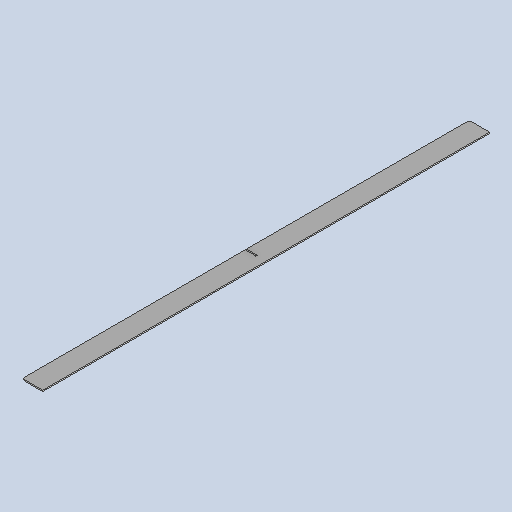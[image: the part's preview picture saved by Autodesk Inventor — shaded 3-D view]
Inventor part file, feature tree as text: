
AUTODESK INVENTOR PART (.ipt)
format: ipt  version: 2025 (Build 290162010, 162A)  size: 127,488 bytes
history: native  units: mm
features: other x3, sheet_metal_op x1, chamfer x1, sketch x1
ambient origin geometry x8: Origin, YZ Plane, XZ Plane, XY Plane, X Axis, Y Axis, Z Axis, Center Point
bodies: Body1 (feature_tree)
feature tree (6):
  other  "BSH 505 amplifier"
  sheet_metal_op  "Face2"
  chamfer  "Corner Round1"
  sketch  "Sketch1"  dims[d15=3.0mm d17=1098.0mm d18=50.0mm d19=3.0mm d20=26.0mm d21=6.0mm]
  other  "Plate2"
  other  "Definition1"
